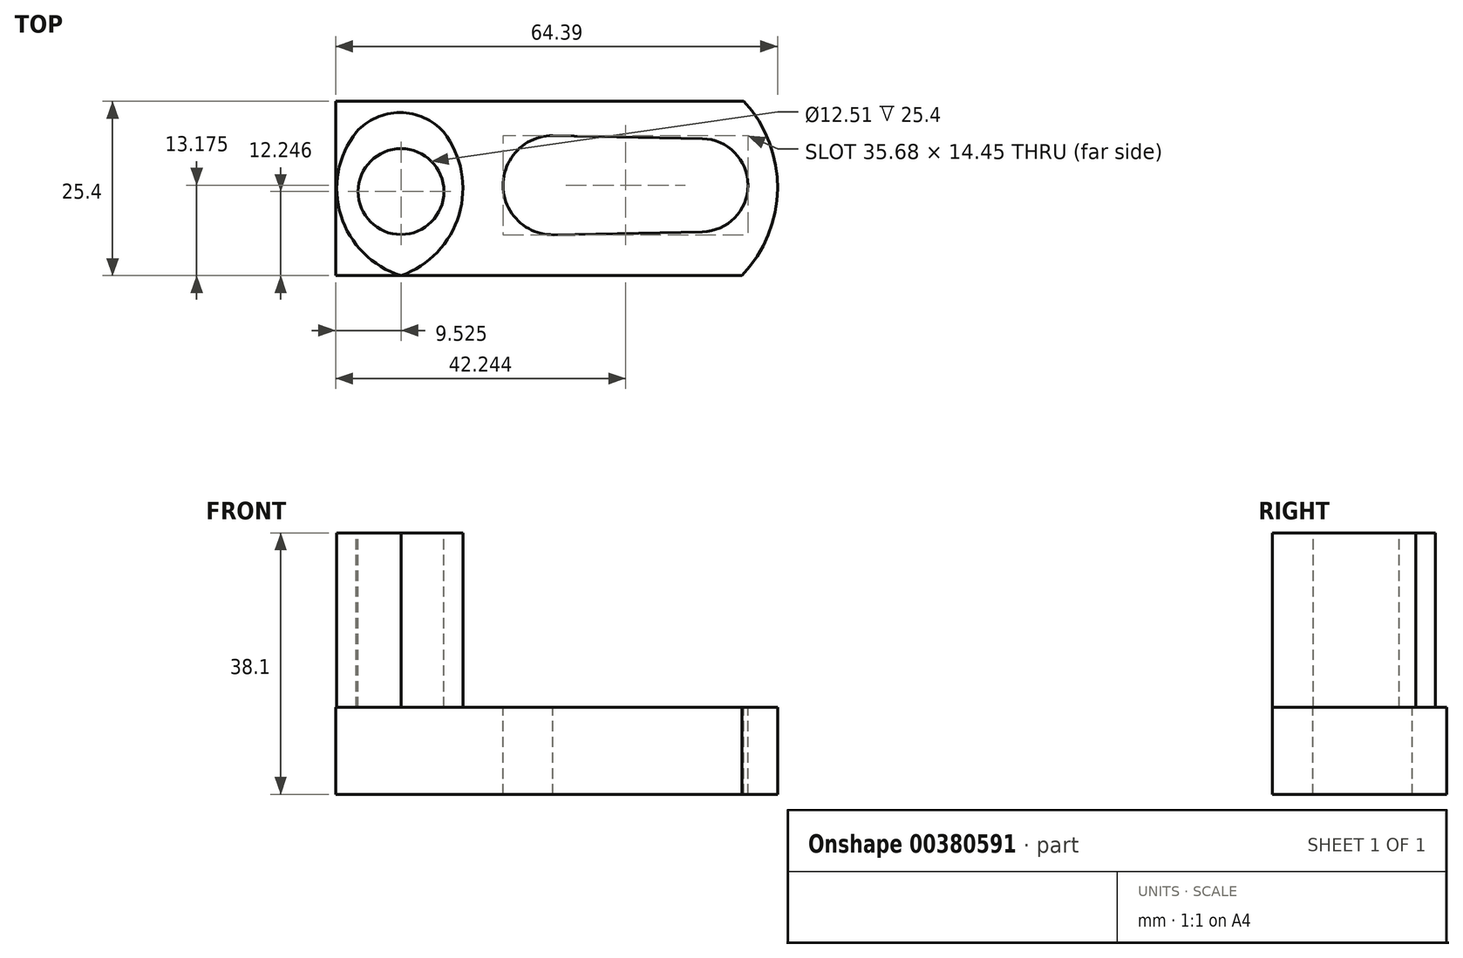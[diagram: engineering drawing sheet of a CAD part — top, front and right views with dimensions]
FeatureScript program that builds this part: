
annotation { "Feature Type Name" : "Feature", "Feature Type Description" : "" }
export const myFeature = defineFeature(function(context is Context, id is Id, definition is map)
    precondition{}
    {
        {
            var Q0;
            Q0=qCreatedBy(makeId("Front.planeOp"),FACE);
            var sketch = newSketch(context, id + "F0", { "sketchPlane" : qUnion([Q0])});
            skLineSegment(sketch, "E0", {"start": v(0, 0) * mm, "end": v(-76.2, 0) * mm});
            skLineSegment(sketch, "E1", {"start": v(-76.2, 0) * mm, "end": v(-76.2, 38.1) * mm});
            skLineSegment(sketch, "E2", {"start": v(-76.2, 38.1) * mm, "end": v(-57.15, 38.1) * mm});
            skLineSegment(sketch, "E3", {"start": v(-57.15, 38.1) * mm, "end": v(-57.15, 12.7) * mm});
            skLineSegment(sketch, "E4", {"start": v(-57.15, 12.7) * mm, "end": v(0, 12.7) * mm});
            skLineSegment(sketch, "E5", {"start": v(0, 12.7) * mm, "end": v(0, 0) * mm});
            skSolve(sketch);
        }
        {
            var Q0;
            Q0=makeQuery(id+"F0.imprint","IMPRINT",FACE,{"disambiguationData":[TD([[makeQuery(id+"F0.imprint","IMPRINT",EDGE,{"derivedFrom":sQuery(id+"F0.wireOp",EDGE,"E0")}),-1.0]])]});
            extrude(context, id + "F1", {"entities" : qUnion([Q0]), "depth" : 25.4 * mm});
        }
        {
            var Q0;
            Q0=makeQuery(id+"F1.opExtrude","SWEPT_FACE",FACE,{"disambiguationData":[OSD([sQuery(id+"F0.wireOp",EDGE,"E2")])]});
            var sketch = newSketch(context, id + "F2", { "sketchPlane" : qUnion([Q0])});
            skCircle(sketch, "E6", {"center": v(-66.68, -13.15) * mm, "radius": 6.26 * mm});
            skPoint(sketch, "E6.centerSnap0", {"position": v(-66.68, 0) * mm});
            skSolve(sketch);
        }
        {
            var Q0;
            Q0=makeQuery(id+"F2.imprint","IMPRINT",FACE,{"disambiguationData":[TD([[makeQuery(id+"F2.imprint","IMPRINT",EDGE,{"derivedFrom":sQuery(id+"F2.wireOp",EDGE,"E6")}),1.0]])]});
            extrude(context, id + "F3", {"entities" : qUnion([Q0]), "operationType" : NewBodyOperationType.REMOVE, "oppositeDirection" : true, "depth" : 25.4 * mm});
        }
        {
            var Q0;
            Q0=makeQuery(id+"F1.opExtrude","SWEPT_FACE",FACE,{"disambiguationData":[OSD([sQuery(id+"F0.wireOp",EDGE,"E4")])]});
            var sketch = newSketch(context, id + "F4", { "sketchPlane" : qUnion([Q0])});
            skCircle(sketch, "E7", {"center": v(-44.57, -12.23) * mm, "radius": 7.23 * mm});
            skCircle(sketch, "E8", {"center": v(-22.9, -12.23) * mm, "radius": 6.79 * mm});
            skLineSegment(sketch, "E9", {"start": v(-44.4, -19.45) * mm, "end": v(-22.77, -19.01) * mm});
            skLineSegment(sketch, "E10", {"start": v(-44.57, -5) * mm, "end": v(-22.77, -5.44) * mm});
            skSolve(sketch);
        }
        {
            var Q0;
            {var subQ0=sQuery(id+"F4.wireOp",EDGE,"E8");var subQ1=makeQuery(id+"F4.imprint","INTERSECT",VERTEX,{"derivedFrom":[subQ0,sQuery(id+"F4.wireOp",EDGE,"E9")]});Q0=makeQuery(id+"F4.imprint","IMPRINT",FACE,{"disambiguationData":[TD([[makeQuery(id+"F4.imprint","IMPRINT",EDGE,{"disambiguationData":[TD([[subQ1,1.0]])],"derivedFrom":subQ0}),1.0]])]});}
            var Q1;
            {var subQ0=sQuery(id+"F4.wireOp",EDGE,"E7");var subQ1=makeQuery(id+"F4.imprint","INTERSECT",VERTEX,{"derivedFrom":[subQ0,sQuery(id+"F4.wireOp",EDGE,"E9")]});Q1=makeQuery(id+"F4.imprint","IMPRINT",FACE,{"disambiguationData":[TD([[makeQuery(id+"F4.imprint","IMPRINT",EDGE,{"disambiguationData":[TD([[subQ1,1.0]])],"derivedFrom":subQ0}),1.0]])]});}
            var Q2;
            {var subQ0=sQuery(id+"F4.wireOp",EDGE,"E9");Q2=makeQuery(id+"F4.imprint","IMPRINT",FACE,{"disambiguationData":[TD([[makeQuery(id+"F4.imprint","IMPRINT",EDGE,{"derivedFrom":subQ0}),1.0]])]});}
            extrude(context, id + "F5", {"entities" : qUnion([Q0, Q1, Q2]), "operationType" : NewBodyOperationType.REMOVE, "oppositeDirection" : true, "depth" : 19.05 * mm});
        }
        {
            var Q0;
            Q0=makeQuery(id+"F1.opExtrude","SWEPT_FACE",FACE,{"disambiguationData":[OSD([sQuery(id+"F0.wireOp",EDGE,"E4")])]});
            var sketch = newSketch(context, id + "F6", { "sketchPlane" : qUnion([Q0])});
            skArc(sketch, "E11", {"start": v(-17.02, -25.4) * mm, "mid": v(-11.8, -12.76) * mm, "end": v(-16.71, 0) * mm});
            skSolve(sketch);
        }
        {
            var Q0;
            {var subQ0=sQuery(id+"F6.wireOp",EDGE,"E11");Q0=makeQuery(id+"F6.imprint","IMPRINT",FACE,{"disambiguationData":[TD([[makeQuery(id+"F6.imprint","IMPRINT",EDGE,{"derivedFrom":subQ0}),-1.0]])]});}
            extrude(context, id + "F7", {"entities" : qUnion([Q0]), "operationType" : NewBodyOperationType.REMOVE, "oppositeDirection" : true, "depth" : 19.05 * mm});
        }
        {
            var Q0;
            Q0=makeQuery(id+"F1.opExtrude","SWEPT_FACE",FACE,{"disambiguationData":[OSD([sQuery(id+"F0.wireOp",EDGE,"E2")])]});
            var sketch = newSketch(context, id + "F8", { "sketchPlane" : qUnion([Q0])});
            skArc(sketch, "E12", {"start": v(-66.68, -25.4) * mm, "mid": v(-57.65, -12.7) * mm, "end": v(-66.68, 0) * mm});
            skArc(sketch, "E13", {"start": v(-66.68, 0) * mm, "mid": v(-76.03, -12.7) * mm, "end": v(-66.68, -25.4) * mm});
            skSolve(sketch);
        }
        {
            var Q0;
            {var subQ0=sQuery(id+"F8.wireOp",EDGE,"E12");Q0=makeQuery(id+"F8.imprint","IMPRINT",FACE,{"disambiguationData":[TD([[makeQuery(id+"F8.imprint","IMPRINT",EDGE,{"derivedFrom":subQ0}),-1.0]])]});}
            var Q1;
            {var subQ0=sQuery(id+"F8.wireOp",EDGE,"E13");Q1=makeQuery(id+"F8.imprint","IMPRINT",FACE,{"disambiguationData":[TD([[makeQuery(id+"F8.imprint","IMPRINT",EDGE,{"derivedFrom":subQ0}),-1.0]])]});}
            var Q2;
            Q2=makeQuery(id+"F8.imprint","IMPRINT",FACE,{"disambiguationData":[TD([[makeQuery(id+"F8.imprint","IMPRINT",EDGE,{"derivedFrom":makeQuery(id+"F3.boolean.opBoolean","COPY",EDGE,{"derivedFrom":makeQuery(id+"F3.opExtrude","CAP_EDGE",EDGE,{"disambiguationData":[OSD([sQuery(id+"F2.wireOp",EDGE,"E6")])],"isStart":true})})}),1.0]])]});
            extrude(context, id + "F9", {"entities" : qUnion([Q0, Q1, Q2]), "operationType" : NewBodyOperationType.REMOVE, "oppositeDirection" : true, "depth" : 25.4 * mm});
        }
        {
            var Q0;
            Q0=makeQuery(id+"F1.opExtrude","SWEPT_FACE",FACE,{"disambiguationData":[OSD([sQuery(id+"F0.wireOp",EDGE,"E2")])]});
            var sketch = newSketch(context, id + "F10", { "sketchPlane" : qUnion([Q0])});
            skArc(sketch, "E14", {"start": v(-60.45, -4.49) * mm, "mid": v(-66.81, -1.64) * mm, "end": v(-73.18, -4.47) * mm});
            skArc(sketch, "E15", {"start": v(-72.76, -21.43) * mm, "mid": v(-66.58, -24.5) * mm, "end": v(-60.58, -21.08) * mm});
            skSolve(sketch);
        }
        {
            var Q0;
            {var subQ0=sQuery(id+"F10.wireOp",EDGE,"E14");Q0=makeQuery(id+"F10.imprint","IMPRINT",FACE,{"disambiguationData":[TD([[makeQuery(id+"F10.imprint","IMPRINT",EDGE,{"derivedFrom":subQ0}),-1.0]])]});}
            var Q1;
            {var subQ0=sQuery(id+"F10.wireOp",EDGE,"E15");var subQ1=makeQuery(id+"F9.boolean.opBoolean","COPY",EDGE,{"derivedFrom":makeQuery(id+"F9.opExtrude","CAP_EDGE",EDGE,{"disambiguationData":[OSD([sQuery(id+"F8.wireOp",EDGE,"E13")])],"isStart":true})});var subQ2=makeQuery(id+"F10.imprint","INTERSECT",VERTEX,{"disambiguationData":[OD(1.0)],"derivedFrom":[subQ1,subQ0]});Q1=makeQuery(id+"F10.imprint","IMPRINT",FACE,{"disambiguationData":[TD([[makeQuery(id+"F10.imprint","IMPRINT",EDGE,{"disambiguationData":[TD([[subQ2,-1.0]])],"derivedFrom":subQ0}),-1.0]])]});}
            extrude(context, id + "F11", {"entities" : qUnion([Q0, Q1]), "operationType" : NewBodyOperationType.REMOVE, "oppositeDirection" : true, "depth" : 25.4 * mm});
        }
    });
